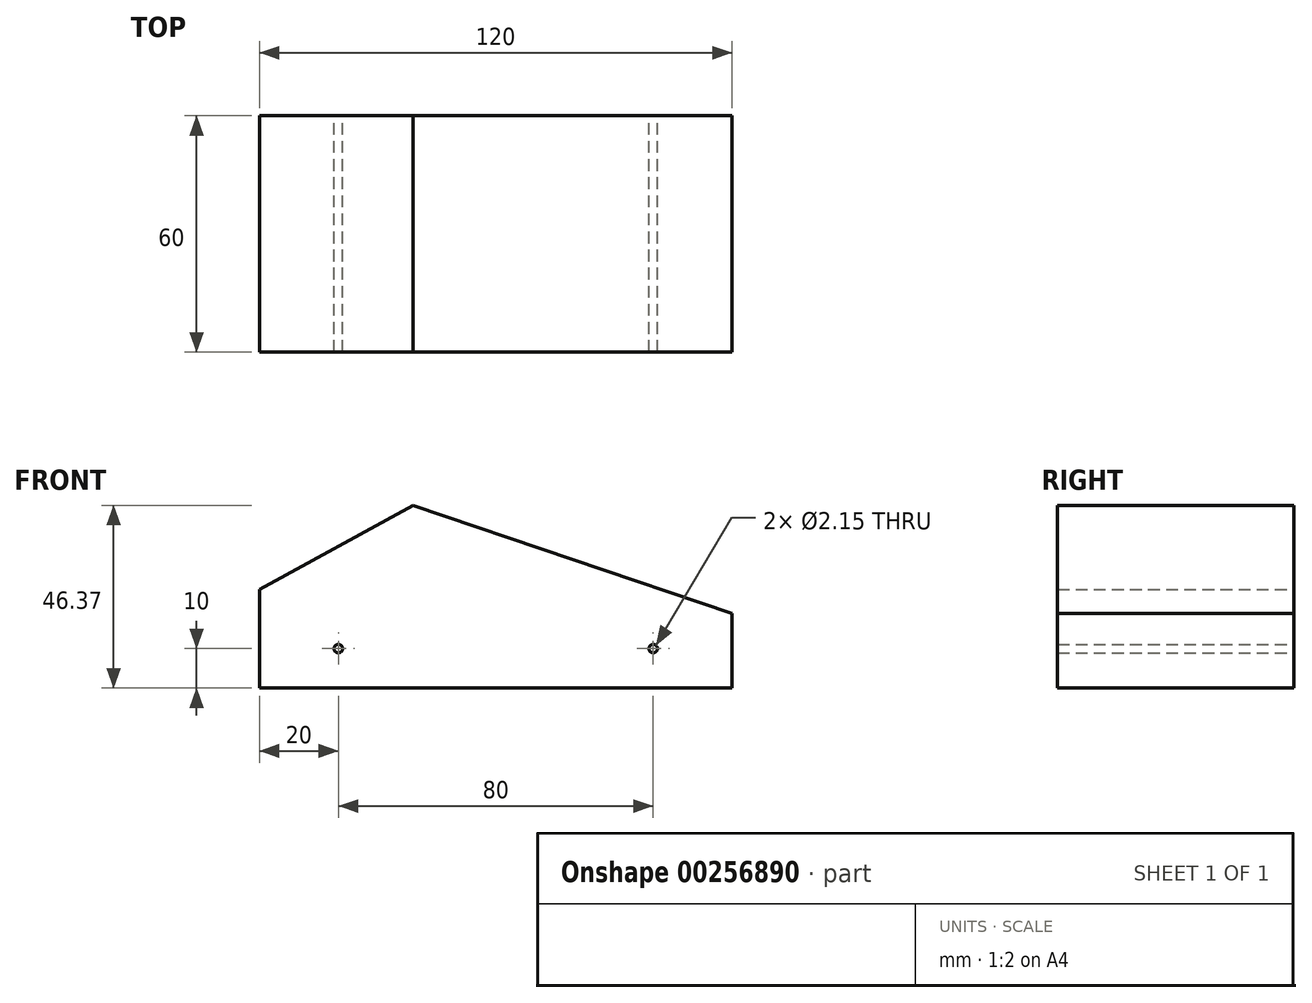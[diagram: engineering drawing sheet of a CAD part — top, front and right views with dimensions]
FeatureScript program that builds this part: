
annotation { "Feature Type Name" : "Feature", "Feature Type Description" : "" }
export const myFeature = defineFeature(function(context is Context, id is Id, definition is map)
    precondition{}
    {
        {
            var Q0;
            Q0=qCreatedBy(makeId("Front.planeOp"),FACE);
            var sketch = newSketch(context, id + "F0", { "sketchPlane" : qUnion([Q0])});
            skLineSegment(sketch, "E0", {"start": v(0, 0) * mm, "end": v(120, 0) * mm});
            skLineSegment(sketch, "E1", {"start": v(0, 0) * mm, "end": v(0, 25) * mm});
            skLineSegment(sketch, "E2", {"start": v(0, 25) * mm, "end": v(39, 46.37) * mm});
            skLineSegment(sketch, "E3", {"start": v(120, 18.92) * mm, "end": v(120, 0) * mm});
            skLineSegment(sketch, "E4", {"start": v(39, 46.37) * mm, "end": v(120, 18.92) * mm});
            skPoint(sketch, "E5.orphan", {"position": v(120, 50) * mm});
            skLineSegment(sketch, "E6", {"start": v(0, 0) * mm, "end": v(20, 0) * mm});
            skLineSegment(sketch, "E7", {"start": v(20, 10) * mm, "end": v(20, 0) * mm});
            skLineSegment(sketch, "E8", {"start": v(120, 0) * mm, "end": v(100, 0) * mm});
            skLineSegment(sketch, "E9", {"start": v(100, 0) * mm, "end": v(100, 10) * mm});
            skCircle(sketch, "E10", {"center": v(20, 10) * mm, "radius": 1.07 * mm});
            skCircle(sketch, "E11", {"center": v(100, 10) * mm, "radius": 1.08 * mm});
            skSolve(sketch);
        }
        {
            var Q0;
            Q0=makeQuery(id+"F0.imprint","IMPRINT",FACE,{"disambiguationData":[TD([[makeQuery(id+"F0.imprint","IMPRINT",EDGE,{"derivedFrom":sQuery(id+"F0.wireOp",EDGE,"E0")}),1.0]])]});
            extrude(context, id + "F1", {"entities" : qUnion([Q0]), "depth" : 60 * mm});
        }
    });
